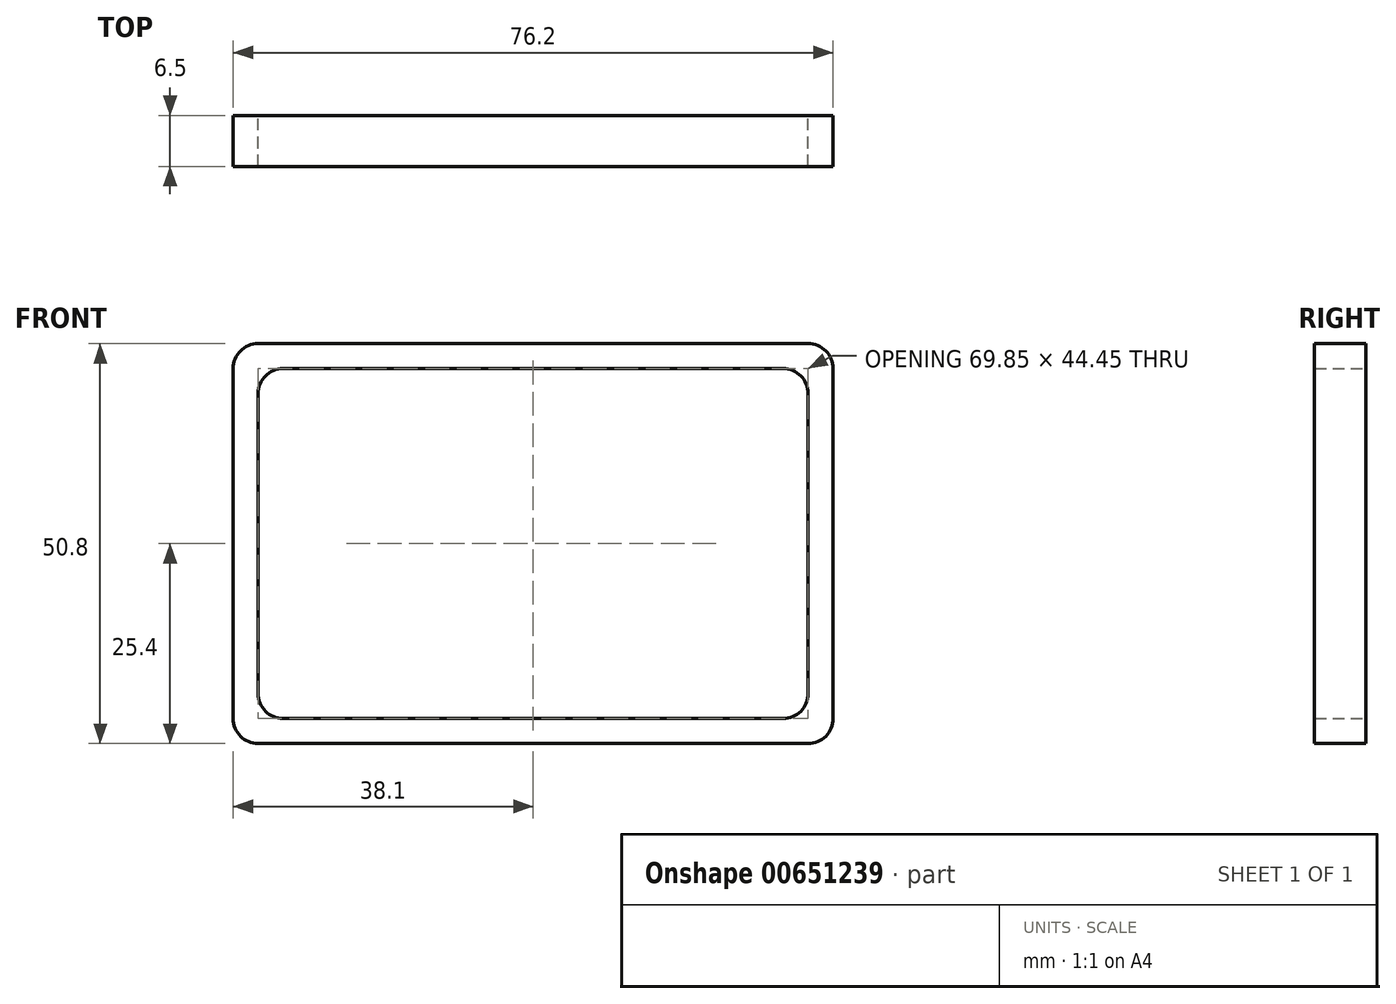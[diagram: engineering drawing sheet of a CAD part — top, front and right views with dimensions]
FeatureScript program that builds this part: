
annotation { "Feature Type Name" : "Feature", "Feature Type Description" : "" }
export const myFeature = defineFeature(function(context is Context, id is Id, definition is map)
    precondition{}
    {
        {
            var Q0;
            Q0=qCreatedBy(makeId("Front.planeOp"),FACE);
            var sketch = newSketch(context, id + "F0", { "sketchPlane" : qUnion([Q0])});
            skLineSegment(sketch, "E0.bottom", {"start": v(38.1, -25.4) * mm, "end": v(-38.1, -25.4) * mm});
            skLineSegment(sketch, "E0.top", {"start": v(38.1, 25.4) * mm, "end": v(-38.1, 25.4) * mm});
            skLineSegment(sketch, "E0.left", {"start": v(38.1, -25.4) * mm, "end": v(38.1, 25.4) * mm});
            skLineSegment(sketch, "E0.right", {"start": v(-38.1, -25.4) * mm, "end": v(-38.1, 25.4) * mm});
            skPoint(sketch, "E0.middle", {"position": v(0, 0) * mm});
            skLineSegment(sketch, "E1.bottom", {"start": v(34.93, -22.23) * mm, "end": v(-34.93, -22.23) * mm});
            skLineSegment(sketch, "E1.top", {"start": v(34.93, 22.23) * mm, "end": v(-34.93, 22.22) * mm});
            skLineSegment(sketch, "E1.left", {"start": v(34.93, -22.23) * mm, "end": v(34.93, 22.23) * mm});
            skLineSegment(sketch, "E1.right", {"start": v(-34.93, -22.23) * mm, "end": v(-34.93, 22.22) * mm});
            skSolve(sketch);
        }
        {
            assignVariable(context, id + "F1", {"name" : "Length", "anyValue" : 6.5});
        }
        {
            var Q0;
            Q0=makeQuery(id+"F0.imprint","IMPRINT",FACE,{"disambiguationData":[TD([[makeQuery(id+"F0.imprint","IMPRINT",EDGE,{"derivedFrom":sQuery(id+"F0.wireOp",EDGE,"E0.bottom")}),-1.0]])]});
            extrude(context, id + "F2", {"entities" : qUnion([Q0]), "depth" : (getVariable(context, 'Length')) * mm, "offsetDistance" : 25.4 * mm});
        }
        {
            var Q0;
            Q0=makeQuery(id+"F2.opExtrude","SWEPT_EDGE",EDGE,{"disambiguationData":[OSD([sQuery(id+"F0.wireOp",EDGE,"E1.top"),sQuery(id+"F0.wireOp",EDGE,"E1.right")])]});
            var Q1;
            Q1=makeQuery(id+"F2.opExtrude","SWEPT_EDGE",EDGE,{"disambiguationData":[OSD([sQuery(id+"F0.wireOp",EDGE,"E1.top"),sQuery(id+"F0.wireOp",EDGE,"E1.left")])]});
            var Q2;
            Q2=makeQuery(id+"F2.opExtrude","SWEPT_EDGE",EDGE,{"disambiguationData":[OSD([sQuery(id+"F0.wireOp",EDGE,"E1.bottom"),sQuery(id+"F0.wireOp",EDGE,"E1.left")])]});
            var Q3;
            Q3=makeQuery(id+"F2.opExtrude","SWEPT_EDGE",EDGE,{"disambiguationData":[OSD([sQuery(id+"F0.wireOp",EDGE,"E1.bottom"),sQuery(id+"F0.wireOp",EDGE,"E1.right")])]});
            var Q4;
            Q4=makeQuery(id+"F2.opExtrude","SWEPT_EDGE",EDGE,{"disambiguationData":[OSD([sQuery(id+"F0.wireOp",EDGE,"E0.top"),sQuery(id+"F0.wireOp",EDGE,"E0.left")])]});
            var Q5;
            Q5=makeQuery(id+"F2.opExtrude","SWEPT_EDGE",EDGE,{"disambiguationData":[OSD([sQuery(id+"F0.wireOp",EDGE,"E0.bottom"),sQuery(id+"F0.wireOp",EDGE,"E0.left")])]});
            var Q6;
            Q6=makeQuery(id+"F2.opExtrude","SWEPT_EDGE",EDGE,{"disambiguationData":[OSD([sQuery(id+"F0.wireOp",EDGE,"E0.bottom"),sQuery(id+"F0.wireOp",EDGE,"E0.right")])]});
            var Q7;
            Q7=makeQuery(id+"F2.opExtrude","SWEPT_EDGE",EDGE,{"disambiguationData":[OSD([sQuery(id+"F0.wireOp",EDGE,"E0.top"),sQuery(id+"F0.wireOp",EDGE,"E0.right")])]});
            fillet(context, id + "F3", {"entities" : qUnion([Q0, Q1, Q2, Q3, Q4, Q5, Q6, Q7]), "radius" : 3.17 * mm, "tangentPropagation" : true, "allowEdgeOverflow" : false});
        }
    });
